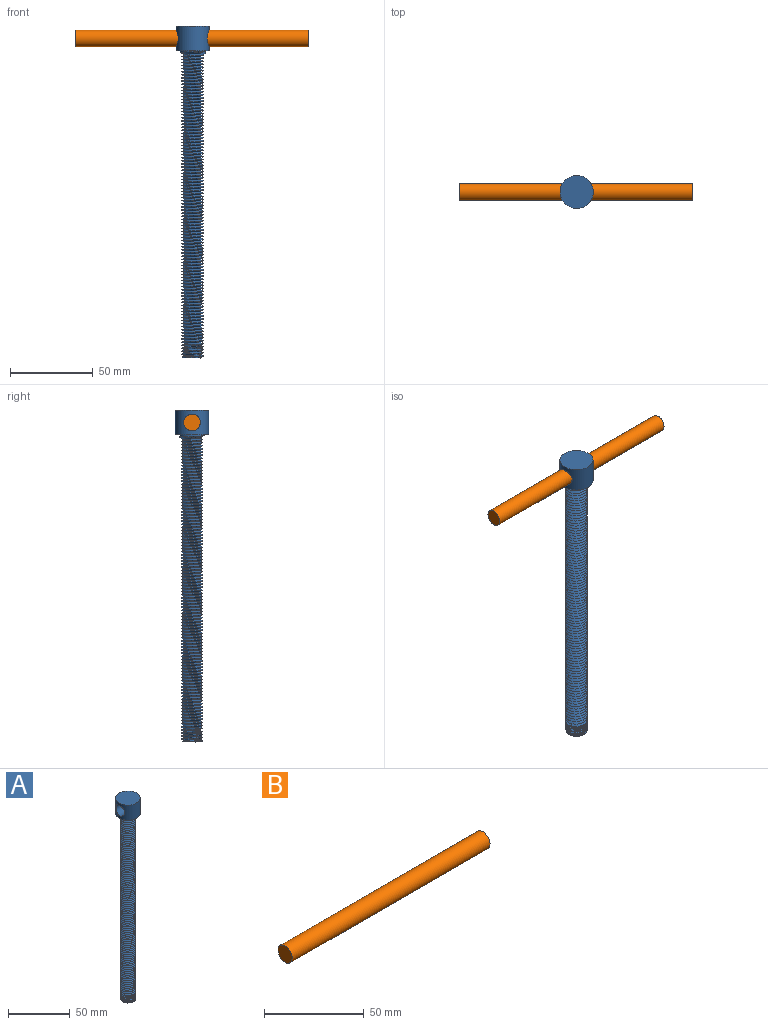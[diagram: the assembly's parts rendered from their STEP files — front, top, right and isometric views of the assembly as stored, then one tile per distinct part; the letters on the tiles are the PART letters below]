
ASSEMBLY  parts=2 mates=1
PART A: 11 faces, bbox 20.2x20.2x201.4 mm
  f0: cylinder r=7.5mm len=15mm, axis (0,0,-1), area 43.6mm2, adj f1,f6,f7
  f1: plane 20x20mm, normal (0,0,-1), area 137.4mm2, adj f0,f2
  f2: cylinder r=10mm len=20mm, axis (0,0,-1), area 779.9mm2, adj f1,f3,f10
  f3: plane 20x20mm, normal (0,0,1), area 314.2mm2, adj f2
  f4: bspline ~185x14.97mm, area 6611.7mm2, adj f5,f6,f7,f8,f9
  f5: bspline ~184.69x14.97mm, area 6518.5mm2, adj f4,f6,f8,f9
  f6: plane 2.62x2.44mm, normal (0,-1,0), area 3.4mm2, adj f0,f4,f5,f7
  f7: bspline ~17.32x15mm, area 51.7mm2, adj f0,f4,f6
  f8: cone r=5.5mm half-angle=45deg, axis (0,0,1), area 15.5mm2, adj f4,f5,f9
  f9: plane 11.23x10.87mm, normal (0,0,-1), area 91mm2, adj f4,f5,f8
  f10: cylinder r=5mm len=20mm, axis (1,0,0), area 628.3mm2, adj f2
PART B: 3 faces, bbox 140x10x10 mm
  f0: plane 10x10mm, normal (1,0,0), area 78.5mm2, adj f1
  f1: cylinder r=5mm len=140mm, axis (1,0,0), area 4398.2mm2, adj f0,f2
  f2: plane 10x10mm, normal (-1,0,0), area 78.5mm2, adj f1
PLACE A at identity fixed
PLACE B rot(axis=(0,-1,-0.08),180deg) t=(-0.38,0,192.5)mm
MATE cylindrical B.f1 <-> A.f10  axis (-1,0,0) through (-0.38,0,192.5)mm
